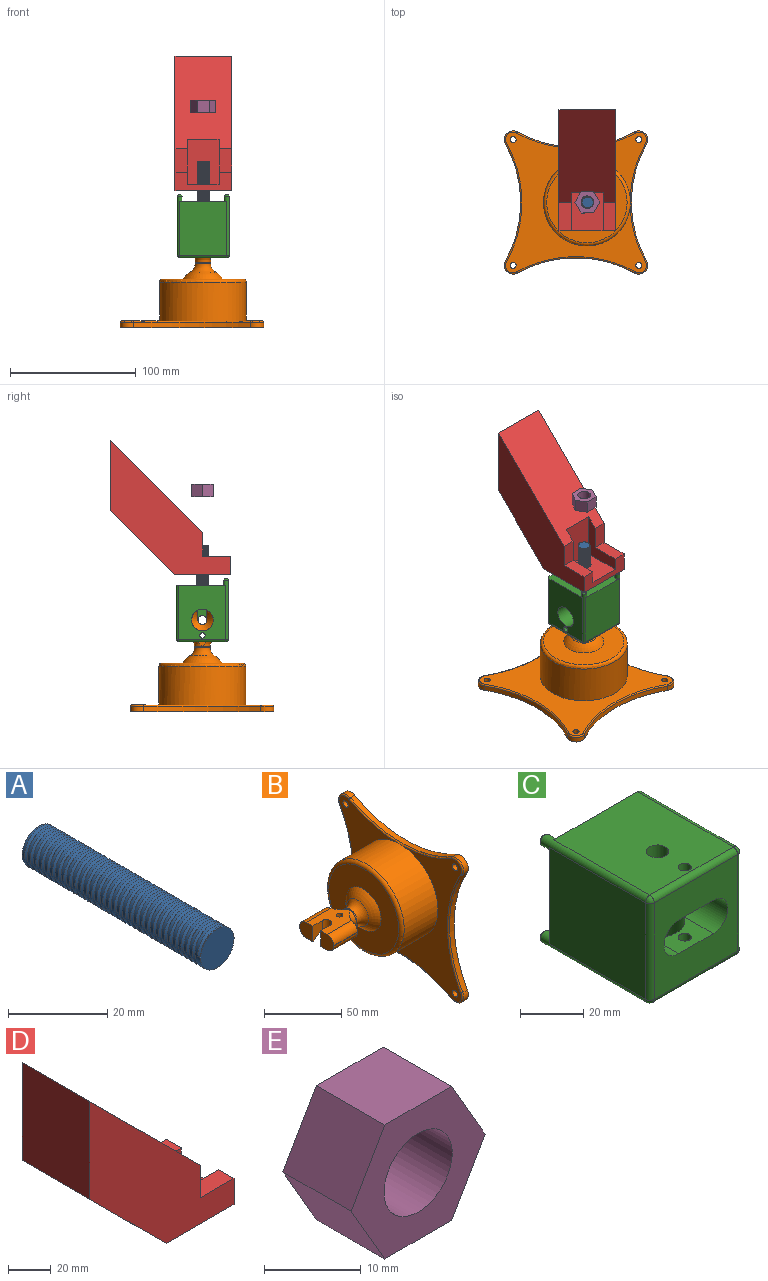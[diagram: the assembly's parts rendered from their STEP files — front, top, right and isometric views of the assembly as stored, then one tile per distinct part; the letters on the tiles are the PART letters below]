
ASSEMBLY  parts=5 mates=6
PART A: 6 faces, bbox 9.8x51.6x11.2 mm
  f0: cylinder r=4.76mm len=50.8mm, axis (0,1,0), area 1210.9mm2, adj f1,f2,f3,f4,f5
  f1: plane 9.53x9.53mm, normal (0,-1,0), area 71.3mm2, adj f0
  f2: plane 9.76x9.28mm, normal (0,1,0), area 67.6mm2, adj f0,f3,f4
  f3: bspline ~50.94x11mm, area 576.4mm2, adj f0,f2,f4,f5
  f4: bspline ~51.2x11mm, area 580.1mm2, adj f0,f2,f3,f5
  f5: plane 0.81x0.5mm, normal (0,0,1), area 0.2mm2, adj f0,f3,f4
PART B: 47 faces, bbox 81.6x115.2x115.2 mm
  f0: plane 114x114mm, normal (1,0,0), area 9492.9mm2, adj f1,f2,f3,f4,f5,f6,f7,f8
  f1: cylinder r=7mm len=10.41mm, axis (1,0,0), area 76.1mm2, adj f0,f2,f8,f13
  f2: cylinder r=95.65mm len=93.18mm, axis (1,0,0), area 408.8mm2, adj f0,f1,f3,f14
  f3: cylinder r=7mm len=10.41mm, axis (1,0,0), area 76.1mm2, adj f0,f2,f4,f15
  f4: cylinder r=95.65mm len=93.18mm, axis (1,0,0), area 408.8mm2, adj f0,f3,f5,f16
  f5: cylinder r=7mm len=10.41mm, axis (1,0,0), area 76.1mm2, adj f0,f4,f6,f17
  f6: cylinder r=95.65mm len=93.18mm, axis (1,0,0), area 408.8mm2, adj f0,f5,f7,f18
  f7: cylinder r=7mm len=10.41mm, axis (1,0,0), area 76.1mm2, adj f0,f6,f8,f19
  f8: cylinder r=95.65mm len=93.18mm, axis (1,0,0), area 408.8mm2, adj f0,f1,f7,f20
  f9: cylinder r=2.4mm len=5.2mm, axis (1,0,0), area 78.5mm2, adj f0,f21
  f10: cylinder r=2.4mm len=5.2mm, axis (1,0,0), area 78.5mm2, adj f0,f21
  f11: cylinder r=2.4mm len=5.2mm, axis (1,0,0), area 78.5mm2, adj f0,f21
  f12: cylinder r=2.4mm len=5.2mm, axis (1,0,0), area 78.5mm2, adj f0,f21
  f13: torus R=6mm, axis (1,0,0), area 27mm2, adj f1,f14,f20,f21
  f14: torus R=96.65mm, axis (-1,0,0), area 153.5mm2, adj f2,f13,f15,f21
  f15: torus R=6mm, axis (1,0,0), area 27mm2, adj f3,f14,f16,f21
  f16: torus R=96.65mm, axis (-1,0,0), area 153.5mm2, adj f4,f15,f17,f21
  f17: torus R=6mm, axis (1,0,0), area 27mm2, adj f5,f16,f18,f21
  f18: torus R=96.65mm, axis (-1,0,0), area 153.5mm2, adj f6,f17,f19,f21
  f19: torus R=6mm, axis (1,0,0), area 27mm2, adj f7,f18,f20,f21
  f20: torus R=96.65mm, axis (-1,0,0), area 152.9mm2, adj f8,f13,f19,f21,f22
  f21: plane 112x112mm, normal (-1,0,0), area 5295.5mm2, adj f9,f10,f11,f12,f13,f14,f15,f16
  f22: cylinder r=34.5mm len=69mm, axis (-1,0,0), area 6698.2mm2, adj f20,f21,f23
  f23: torus R=32mm, axis (-1,0,0), area 828.8mm2, adj f22,f24
  f24: plane 64x64mm, normal (-1,0,0), area 2426.5mm2, adj f23,f25
  f25: torus R=0.17mm, axis (1,0,0), area 678.1mm2, adj f24,f26
  f26: torus R=14.17mm, axis (-1,0,0), area 384.8mm2, adj f25,f27
  f27: cylinder r=6.17mm len=12.34mm, axis (-1,0,0), area 23.7mm2, adj f26,f32,f33
  f28: plane 9.56x2.16mm, normal (1,0,0), area 9.3mm2, adj f29,f31,f33,f34
  f29: plane 21.91x0.34mm, normal (0,1,0), area 7.5mm2, adj f28,f31,f34,f35
  f30: plane 9.56x2.16mm, normal (1,0,0), area 9.3mm2, adj f32,f38,f39,f40
  f31: cylinder r=6mm len=22.43mm, axis (-1,0,0), area 207.6mm2, adj f28,f29,f33,f35,f41
  f32: torus R=14.17mm, axis (-1,0,0), area 178.6mm2, adj f27,f30,f38,f40,f41,f44
  f33: torus R=14.17mm, axis (-1,0,0), area 178.6mm2, adj f27,f28,f31,f34,f41,f44
  f34: cylinder r=6mm len=22.43mm, axis (-1,0,0), area 207.6mm2, adj f28,f29,f33,f35,f44
  f35: plane 12.34x11.9mm, normal (-1,0,0), area 131.4mm2, adj f29,f31,f34,f36,f41,f44
  f36: plane 12.34x8.75mm, normal (0,-1,0), area 84.2mm2, adj f35,f41,f42,f43,f44
  f37: cylinder r=2.1mm len=12.34mm, axis (0,0,-1), area 162.9mm2, adj f41,f44
  f38: cylinder r=6mm len=22.43mm, axis (-1,0,0), area 207.6mm2, adj f30,f32,f39,f44,f45
  f39: plane 21.91x0.34mm, normal (0,-1,0), area 7.5mm2, adj f30,f38,f40,f45
  f40: cylinder r=6mm len=22.43mm, axis (-1,0,0), area 207.6mm2, adj f30,f32,f39,f41,f45
  f41: plane 29.91x19.01mm, normal (0,0,-1), area 234.6mm2, adj f31,f32,f33,f35,f36,f37,f40,f42
  f42: cone r=6.1mm half-angle=45deg, axis (0,0,-1), area 214.9mm2, adj f36,f41,f43,f46
  f43: cylinder r=3.6mm len=7.34mm, axis (0,0,1), area 83mm2, adj f36,f42,f44,f46
  f44: plane 29.91x19mm, normal (0,0,1), area 386.7mm2, adj f32,f33,f34,f35,f36,f37,f38,f43
  f45: plane 12.34x11.9mm, normal (-1,0,0), area 131.4mm2, adj f38,f39,f40,f41,f44,f46
  f46: plane 12.34x8.75mm, normal (0,1,0), area 84.2mm2, adj f41,f42,f43,f44,f45
PART C: 34 faces, bbox 41.5x50x41.5 mm
  f0: plane 28.6x13mm, normal (0,-1,0), area 329.1mm2, adj f1,f3,f4,f5,f8
  f1: plane 26x15.6mm, normal (0,0,-1), area 352.2mm2, adj f0,f3,f5,f7,f10,f11
  f2: plane 2x2mm, normal (0,1,0), area 3.1mm2, adj f12
  f3: cylinder r=6.5mm len=26mm, axis (0,1,0), area 526.2mm2, adj f0,f1,f4,f6,f7,f17
  f4: plane 15.6x4.9mm, normal (0,0,1), area 22.3mm2, adj f0,f3,f5,f17
  f5: cylinder r=6.5mm len=26mm, axis (0,1,0), area 526.2mm2, adj f0,f1,f4,f6,f7,f17
  f6: plane 15.6x13.4mm, normal (0,0,1), area 141mm2, adj f3,f5,f7,f17,f18
  f7: plane 37.48x37.48mm, normal (0,-1,0), area 1069mm2, adj f1,f3,f5,f6,f9,f15,f19,f20
  f8: cone r=2.38mm half-angle=59deg, axis (0,1,0), area 75.6mm2, adj f0,f21
  f9: cylinder r=2mm len=37.48mm, axis (-1,0,0), area 117.7mm2, adj f7,f13,f16,f22
  f10: cylinder r=3.55mm len=14.24mm, axis (0,0,-1), area 317.6mm2, adj f1,f22
  f11: cylinder r=2.1mm len=14.24mm, axis (0,0,1), area 187.9mm2, adj f1,f22
  f12: cone r=1.5mm half-angle=45deg, axis (0,-1,0), area 13.3mm2, adj f2,f23
  f13: sphere r=2mm, area 6.3mm2, adj f9,f20,f23
  f14: sphere r=2mm, area 6.3mm2, adj f15,f19,f24
  f15: cylinder r=2mm len=37.48mm, axis (0,0,1), area 117.7mm2, adj f7,f14,f16,f25
  f16: sphere r=2mm, area 6.3mm2, adj f9,f15,f26
  f17: cylinder r=8.7mm len=17.4mm, axis (0,0,1), area 778.8mm2, adj f3,f4,f5,f6,f27
  f18: cylinder r=2.1mm len=14.24mm, axis (0,0,1), area 187.9mm2, adj f6,f27
  f19: cylinder r=2mm len=37.48mm, axis (1,0,0), area 117.7mm2, adj f7,f14,f27,f28
  f20: cylinder r=2mm len=37.48mm, axis (0,0,-1), area 117.7mm2, adj f7,f13,f28,f29
  f21: cylinder r=4.76mm len=17mm, axis (0,-1,0), area 508.7mm2, adj f8,f30
  f22: plane 43x37.48mm, normal (0,0,1), area 1558.1mm2, adj f9,f10,f11,f23,f26,f30
  f23: cylinder r=2mm len=47mm, axis (0,1,0), area 185.4mm2, adj f12,f13,f22,f29,f30
  f24: cylinder r=2mm len=43mm, axis (0,-1,0), area 135.1mm2, adj f14,f25,f27,f30
  f25: plane 43x37.48mm, normal (1,0,0), area 1611.5mm2, adj f15,f24,f26,f30
  f26: cylinder r=2mm len=43mm, axis (0,-1,0), area 135.1mm2, adj f16,f22,f25,f30
  f27: plane 43x37.48mm, normal (0,0,-1), area 1359.9mm2, adj f17,f18,f19,f24,f30,f32
  f28: sphere r=2mm, area 6.3mm2, adj f19,f20,f32
  f29: plane 43x37.48mm, normal (-1,0,0), area 1611.5mm2, adj f20,f23,f30,f32
  f30: plane 41.48x41.48mm, normal (0,1,0), area 1620.5mm2, adj f21,f22,f23,f24,f25,f26,f27,f29
  f31: plane 2x2mm, normal (0,1,0), area 3.1mm2, adj f33
  f32: cylinder r=2mm len=47mm, axis (0,1,0), area 185.4mm2, adj f27,f28,f29,f30,f33
  f33: cone r=1.5mm half-angle=45deg, axis (0,-1,0), area 13.3mm2, adj f31,f32
PART D: 20 faces, bbox 95.9x45x107.2 mm
  f0: plane 45x45mm, normal (0,0,-1), area 1890.7mm2, adj f5,f6,f9,f10,f11,f16,f18
  f1: plane 22.37x10mm, normal (0,0,1), area 223.7mm2, adj f2,f6,f9,f12
  f2: plane 18.58x10mm, normal (1,0,0), area 185.8mm2, adj f1,f3,f9,f12
  f3: plane 73.57x73.57mm, normal (0.71,0,0.71), area 4412.3mm2, adj f2,f4,f8,f9,f10,f12,f13,f14
  f4: plane 18.58x10mm, normal (1,0,0), area 185.8mm2, adj f3,f7,f10,f13
  f5: plane 50.94x50.94mm, normal (-0.71,0,-0.71), area 3241.9mm2, adj f0,f8,f9,f10
  f6: plane 45x15mm, normal (1,0,0), area 425mm2, adj f0,f1,f7,f9,f10,f12,f13,f15
  f7: plane 22.37x10mm, normal (0,0,1), area 223.7mm2, adj f4,f6,f10,f13
  f8: plane 56.21x45mm, normal (-1,0,0), area 2529.5mm2, adj f3,f5,f9,f10
  f9: plane 107.15x95.94mm, normal (0,-1,0), area 4215mm2, adj f0,f1,f2,f3,f5,f6,f8
  f10: plane 107.15x95.94mm, normal (0,1,0), area 4215mm2, adj f0,f3,f4,f5,f6,f7,f8
  f11: cylinder r=5.5mm len=11mm, axis (0,0,-1), area 172.8mm2, adj f0,f15
  f12: plane 36.21x30mm, normal (0,1,0), area 470.9mm2, adj f1,f2,f3,f6,f14,f15
  f13: plane 36.21x30mm, normal (0,-1,0), area 470.9mm2, adj f3,f4,f6,f7,f14,f15
  f14: plane 36.21x25mm, normal (1,0,0), area 905.3mm2, adj f3,f12,f13,f15
  f15: plane 30x25mm, normal (0,0,1), area 655mm2, adj f6,f11,f12,f13,f14
  f16: cylinder r=2.5mm len=5mm, axis (0,0,-1), area 78.5mm2, adj f0,f17
  f17: plane 5x5mm, normal (0,0,-1), area 19.6mm2, adj f16
  f18: cylinder r=2.5mm len=5mm, axis (0,0,-1), area 78.5mm2, adj f0,f19
  f19: plane 5x5mm, normal (0,0,-1), area 19.6mm2, adj f18
PART E: 9 faces, bbox 19.6x10x17 mm
  f0: plane 10x8.5mm, normal (0.87,0,0.5), area 98.1mm2, adj f1,f6,f7,f8
  f1: plane 10x9.82mm, normal (0,0,1), area 98.1mm2, adj f0,f2,f7,f8
  f2: plane 10x8.5mm, normal (-0.87,0,0.5), area 98.1mm2, adj f1,f3,f7,f8
  f3: plane 10x8.5mm, normal (-0.87,0,-0.5), area 98.1mm2, adj f2,f4,f7,f8
  f4: plane 10x9.82mm, normal (0,0,-1), area 98.1mm2, adj f3,f6,f7,f8
  f5: cylinder r=5mm len=10mm, axis (0,1,0), area 314.2mm2, adj f7,f8
  f6: plane 10x8.5mm, normal (0.87,0,-0.5), area 98.1mm2, adj f0,f4,f7,f8
  f7: plane 19.63x17mm, normal (0,-1,0), area 171.7mm2, adj f0,f1,f2,f3,f4,f5,f6
  f8: plane 19.63x17mm, normal (0,1,0), area 171.7mm2, adj f0,f1,f2,f3,f4,f5,f6
PLACE A rot(axis=(0.1,0.7,0.7),168.7deg) t=(-99.67,-32.44,-106.11)mm
PLACE B rot(axis=(0,1,0),90deg) t=(-108.66,-32.33,-232.88)mm
PLACE C rot(axis=(0.58,0.58,0.58),120deg) t=(-99.67,-32.44,-182.48)mm fixed
PLACE D rot(axis=(0,0,-1),90deg) t=(-77.17,-25.3,-129.4)mm
PLACE E rot(axis=(0,-0.71,-0.71),179.6deg) t=(-99.67,-32.44,-57.16)mm
MATE cylindrical C.f12 <-> D.f16  axis (0,0,1) through (-80.94,-51.18,-133.48)mm
MATE cylindrical A.f0 <-> D.f11  axis (0,0,1) through (-99.67,-32.44,-106.11)mm
MATE cylindrical D.f11 <-> E.f5  axis (0,0,1) through (-99.67,-32.44,-124.4)mm
MATE cylindrical C.f11 <-> B.f37  axis (-1,0,0) through (-120.41,-32.44,-177.48)mm
MATE cylindrical C.f32 <-> D.f18  axis (0,0,1) through (-118.41,-51.18,-133.48)mm
MATE planar B.f41 <-> C.f11  axis (-1,0,0) through (-106.17,-36.68,-181.99)mm
